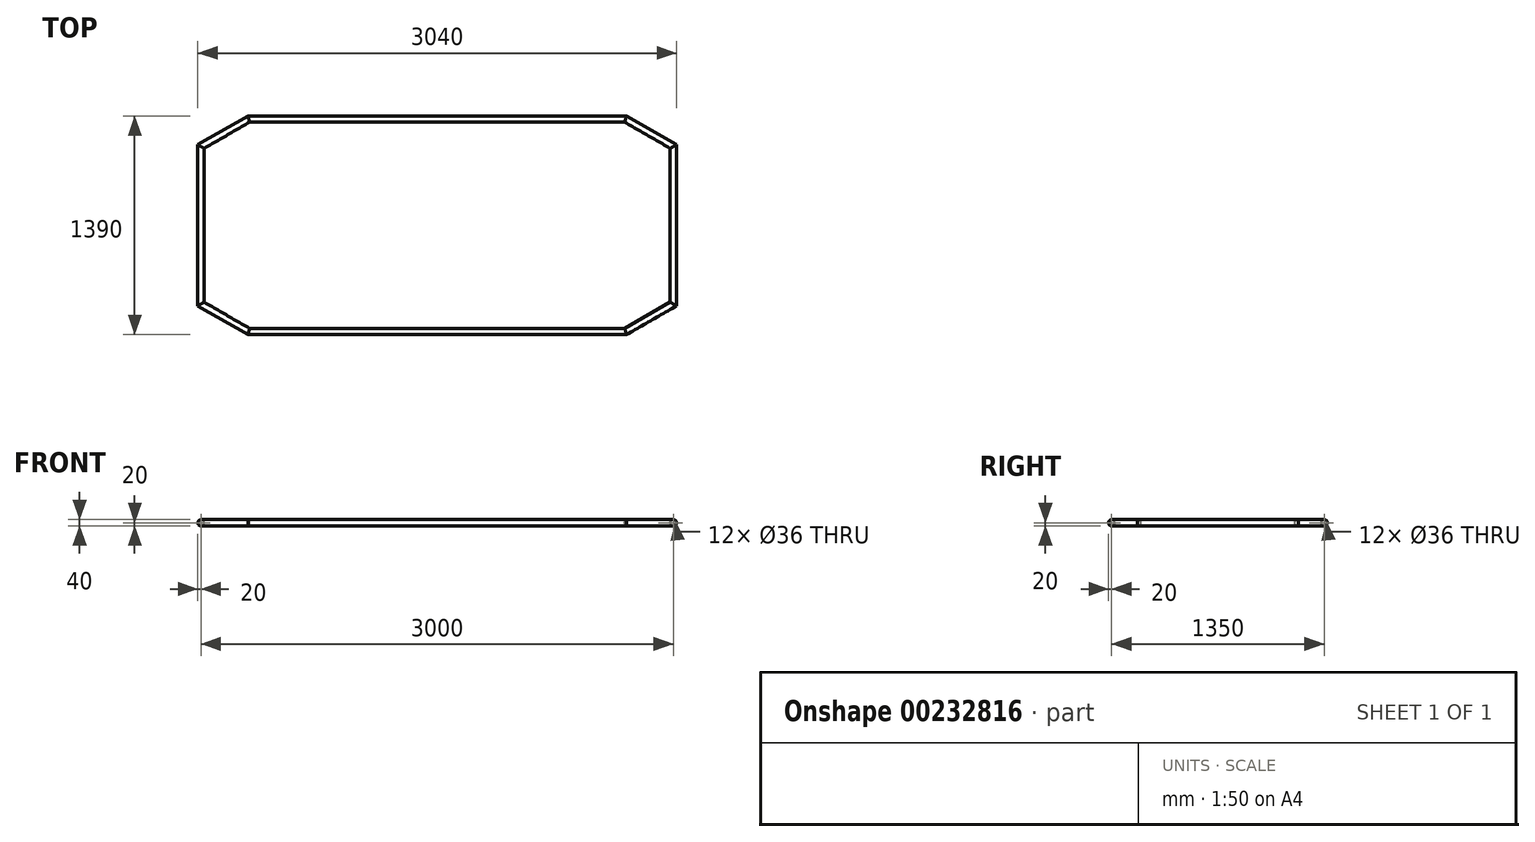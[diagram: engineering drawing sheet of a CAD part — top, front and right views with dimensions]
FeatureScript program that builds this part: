
annotation { "Feature Type Name" : "Feature", "Feature Type Description" : "" }
export const myFeature = defineFeature(function(context is Context, id is Id, definition is map)
    precondition{}
    {
        {
            var Q0;
            Q0=qCreatedBy(makeId("Top.planeOp"),FACE);
            var sketch = newSketch(context, id + "F0", { "sketchPlane" : qUnion([Q0])});
            skLineSegment(sketch, "E0", {"start": v(-1500, 0) * mm, "end": v(-1500, 500) * mm});
            skLineSegment(sketch, "E1", {"start": v(-1500, 500) * mm, "end": v(-1196.9, 675) * mm});
            skLineSegment(sketch, "E2", {"start": v(-1196.9, 675) * mm, "end": v(1196.9, 675) * mm});
            skLineSegment(sketch, "E3", {"start": v(1196.9, 675) * mm, "end": v(1500, 500) * mm});
            skLineSegment(sketch, "E4", {"start": v(1500, 500) * mm, "end": v(1500, 0) * mm});
            skLineSegment(sketch, "E5", {"start": v(-1500, 0) * mm, "end": v(1500, 0) * mm, "construction": true});
            skLineSegment(sketch, "E6.MirrorCS", {"start": v(-1500, -500) * mm, "end": v(-1196.9, -675) * mm});
            skLineSegment(sketch, "E7.MirrorCS", {"start": v(1196.9, -675) * mm, "end": v(1500, -500) * mm});
            skLineSegment(sketch, "E8.MirrorCS", {"start": v(-1196.9, -675) * mm, "end": v(1196.9, -675) * mm});
            skLineSegment(sketch, "E9.MirrorCS", {"start": v(1500, -500) * mm, "end": v(1500, 0) * mm});
            skLineSegment(sketch, "E10.MirrorCS", {"start": v(-1500, 0) * mm, "end": v(-1500, -500) * mm});
            skSolve(sketch);
        }
        {
            var Q0;
            Q0=qCreatedBy(makeId("Front.planeOp"),FACE);
            var sketch = newSketch(context, id + "F1", { "sketchPlane" : qUnion([Q0])});
            skCircle(sketch, "E11", {"center": v(-1500, 0) * mm, "radius": 20 * mm});
            skCircle(sketch, "E12", {"center": v(-1500, 0) * mm, "radius": 18 * mm});
            skSolve(sketch);
        }
        {
            var Q0;
            Q0=makeQuery(id+"F1.imprint","IMPRINT",FACE,{"disambiguationData":[TD([[makeQuery(id+"F1.imprint","IMPRINT",EDGE,{"derivedFrom":sQuery(id+"F1.wireOp",EDGE,"E11")}),1.0]])]});
            var Q1;
            Q1=sQuery(id+"F0.wireOp",EDGE,"E0");
            var Q2;
            Q2=sQuery(id+"F0.wireOp",EDGE,"E1");
            var Q3;
            Q3=sQuery(id+"F0.wireOp",EDGE,"E2");
            var Q4;
            Q4=sQuery(id+"F0.wireOp",EDGE,"E3");
            var Q5;
            Q5=sQuery(id+"F0.wireOp",EDGE,"E4");
            var Q6;
            Q6=sQuery(id+"F0.wireOp",EDGE,"E9.MirrorCS");
            var Q7;
            Q7=sQuery(id+"F0.wireOp",EDGE,"E7.MirrorCS");
            var Q8;
            Q8=sQuery(id+"F0.wireOp",EDGE,"E8.MirrorCS");
            var Q9;
            Q9=sQuery(id+"F0.wireOp",EDGE,"E6.MirrorCS");
            var Q10;
            Q10=sQuery(id+"F0.wireOp",EDGE,"E10.MirrorCS");
            sweep(context, id + "F2", {"profiles" : qUnion([Q0]), "path" : qUnion([Q1, Q2, Q3, Q4, Q5, Q6, Q7, Q8, Q9, Q10])});
        }
    });
